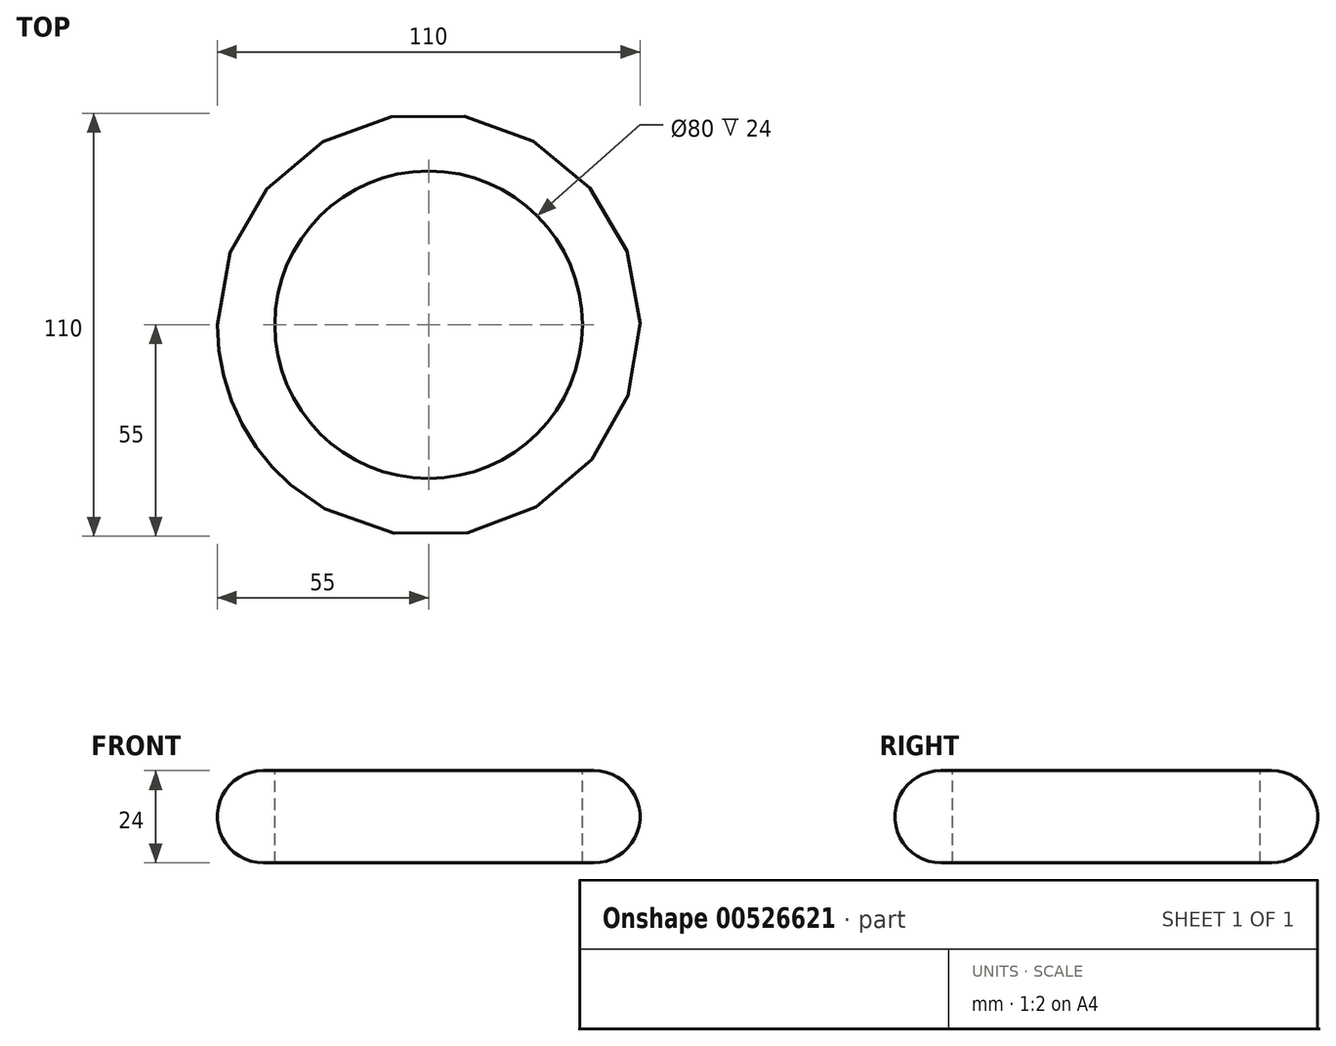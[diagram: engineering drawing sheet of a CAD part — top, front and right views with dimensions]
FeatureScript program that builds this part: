
annotation { "Feature Type Name" : "Feature", "Feature Type Description" : "" }
export const myFeature = defineFeature(function(context is Context, id is Id, definition is map)
    precondition{}
    {
        {
            var Q0;
            Q0=qCreatedBy(makeId("Top.planeOp"),FACE);
            var sketch = newSketch(context, id + "F0", { "sketchPlane" : qUnion([Q0])});
            skCircle(sketch, "E0", {"center": v(0, 0) * mm, "radius": 40 * mm});
            skSolve(sketch);
        }
        {
            var Q0;
            Q0=qCreatedBy(makeId("Front.planeOp"),FACE);
            var sketch = newSketch(context, id + "F1", { "sketchPlane" : qUnion([Q0])});
            skArc(sketch, "E1", {"start": v(-43, 12) * mm, "mid": v(-55, 0) * mm, "end": v(-43, -12) * mm});
            skLineSegment(sketch, "E2", {"start": v(-43, 12) * mm, "end": v(-40, 12) * mm});
            skLineSegment(sketch, "E3", {"start": v(-40, 12) * mm, "end": v(-40, -12) * mm});
            skLineSegment(sketch, "E4", {"start": v(-40, -12) * mm, "end": v(-43, -12) * mm});
            skSolve(sketch);
        }
        {
            var Q0;
            Q0 = qSketchRegion(id + "F1", true);
            var Q1;
            Q1 = qConstructionFilter(qBodyType(qCreatedBy(id + "F0" ,EDGE), BodyType.WIRE), ConstructionObject.NO);
            sweep(context, id + "F2", {"profiles" : qUnion([Q0]), "path" : qUnion([Q1])});
        }
        {
            var Q0;
            Q0=qCreatedBy(makeId("Right.planeOp"),FACE);
            cPlane(context, id + "F3", {"entities" : qUnion([Q0]), "cplaneType" : CPlaneType.OFFSET, "offset" : 40 * mm, "width" : 150 * mm, "height" : 150 * mm});
        }
        {
            var Q0;
            Q0=qCreatedBy(makeId("Right.planeOp"),FACE);
            cPlane(context, id + "F4", {"entities" : qUnion([Q0]), "cplaneType" : CPlaneType.OFFSET, "offset" : 14 * mm, "width" : 150 * mm, "height" : 150 * mm});
        }
    });
